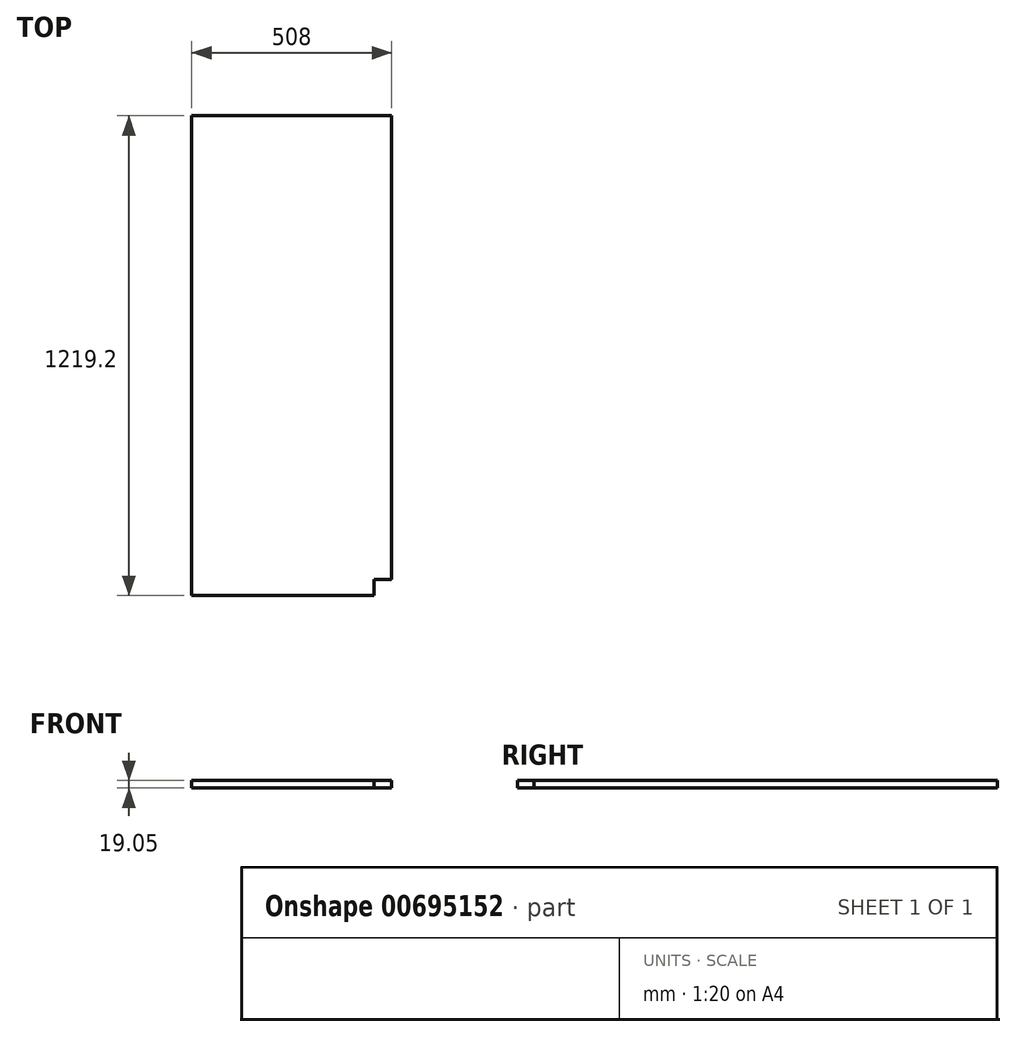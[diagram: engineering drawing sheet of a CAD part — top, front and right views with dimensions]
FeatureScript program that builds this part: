
annotation { "Feature Type Name" : "Feature", "Feature Type Description" : "" }
export const myFeature = defineFeature(function(context is Context, id is Id, definition is map)
    precondition{}
    {
        {
            var Q0;
            Q0=qCreatedBy(makeId("Top.planeOp"),FACE);
            var sketch = newSketch(context, id + "F0", { "sketchPlane" : qUnion([Q0])});
            skLineSegment(sketch, "E0.bottom", {"start": v(242.38, -694.63) * mm, "end": v(705.93, -694.63) * mm});
            skLineSegment(sketch, "E0.top", {"start": v(242.38, 524.57) * mm, "end": v(750.38, 524.57) * mm});
            skLineSegment(sketch, "E0.left", {"start": v(242.38, -694.63) * mm, "end": v(242.38, 524.57) * mm});
            skLineSegment(sketch, "E0.right", {"start": v(750.38, -653.36) * mm, "end": v(750.38, 524.57) * mm});
            skLineSegment(sketch, "E1", {"start": v(705.93, -694.63) * mm, "end": v(705.93, -653.36) * mm});
            skLineSegment(sketch, "E2", {"start": v(705.93, -653.36) * mm, "end": v(750.38, -653.36) * mm});
            skSolve(sketch);
        }
        {
            var Q0;
            Q0=makeQuery(id+"F0.imprint","IMPRINT",FACE,{"disambiguationData":[TD([[makeQuery(id+"F0.imprint","IMPRINT",EDGE,{"derivedFrom":sQuery(id+"F0.wireOp",EDGE,"E0.bottom")}),1.0]])]});
            extrude(context, id + "F1", {"entities" : qUnion([Q0]), "depth" : 19.05 * mm, "offsetDistance" : 25.4 * mm});
        }
    });
